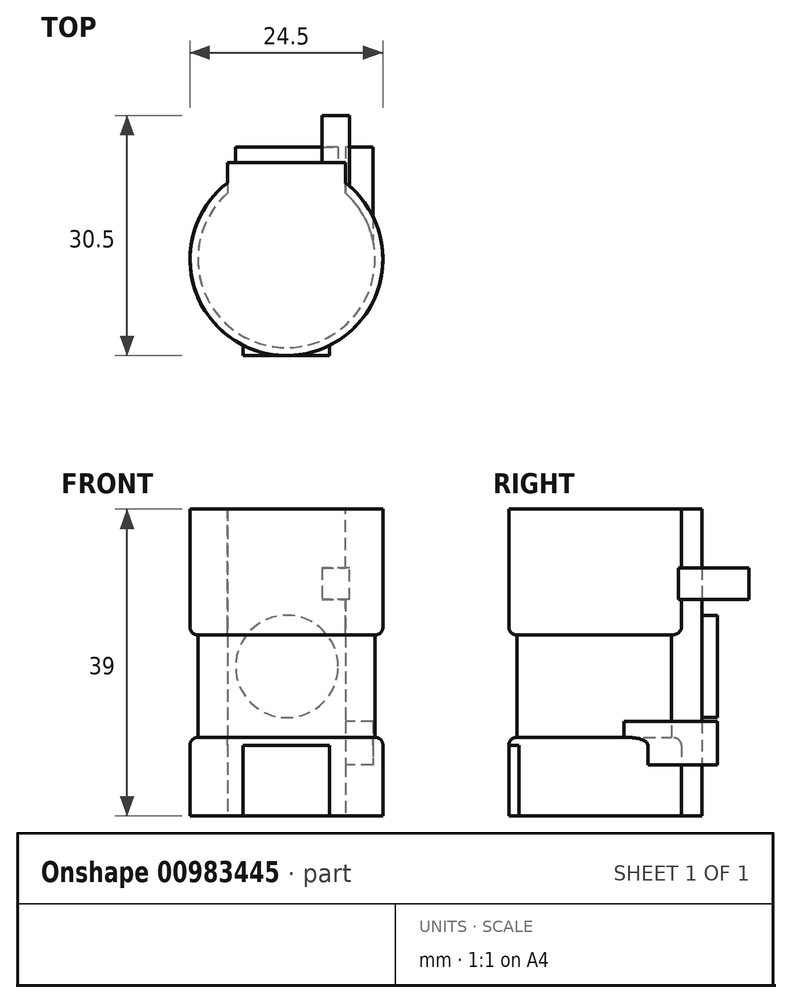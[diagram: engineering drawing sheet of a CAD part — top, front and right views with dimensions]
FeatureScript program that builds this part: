
annotation { "Feature Type Name" : "Feature", "Feature Type Description" : "" }
export const myFeature = defineFeature(function(context is Context, id is Id, definition is map)
    precondition{}
    {
        {
            var Q0;
            Q0=qCreatedBy(makeId("Top.planeOp"),FACE);
            var sketch = newSketch(context, id + "F0", { "sketchPlane" : qUnion([Q0])});
            skCircle(sketch, "E0", {"center": v(0, 0) * mm, "radius": 11.25 * mm});
            skSolve(sketch);
        }
        {
            var Q0;
            Q0 = qSketchRegion(id + "F0", true);
            extrude(context, id + "F1", {"entities" : qUnion([Q0]), "depth" : 39 * mm, "offsetDistance" : 25 * mm});
        }
        {
            var Q0;
            Q0=makeQuery(id+"F1.opExtrude","CAP_FACE",FACE,{"disambiguationData":[OSD([sQuery(id+"F0.wireOp",EDGE,"E0")])],"isStart":false});
            var sketch = newSketch(context, id + "F2", { "sketchPlane" : qUnion([Q0])});
            skCircle(sketch, "E1", {"center": v(0, 0) * mm, "radius": 12.25 * mm});
            skSolve(sketch);
        }
        {
            var Q0;
            Q0=makeQuery(id+"F2.imprint","IMPRINT",FACE,{"disambiguationData":[TD([[makeQuery(id+"F2.imprint","IMPRINT",EDGE,{"derivedFrom":sQuery(id+"F2.wireOp",EDGE,"E1")}),1.0]])]});
            extrude(context, id + "F3", {"entities" : qUnion([Q0]), "operationType" : NewBodyOperationType.ADD, "oppositeDirection" : true, "depth" : 16 * mm, "offsetDistance" : 25 * mm});
        }
        {
            var Q0;
            Q0=makeQuery(id+"F1.opExtrude","CAP_FACE",FACE,{"disambiguationData":[OSD([sQuery(id+"F0.wireOp",EDGE,"E0")])],"isStart":true});
            var sketch = newSketch(context, id + "F4", { "sketchPlane" : qUnion([Q0])});
            skCircle(sketch, "E2", {"center": v(0, 0) * mm, "radius": 12.25 * mm});
            skSolve(sketch);
        }
        {
            var Q0;
            Q0=makeQuery(id+"F3.opExtrude","CAP_EDGE",EDGE,{"disambiguationData":[OSD([sQuery(id+"F2.wireOp",EDGE,"E1")])],"isStart":false});
            fillet(context, id + "F5", {"entities" : qUnion([Q0]), "radius" : 1 * mm, "tangentPropagation" : true, "allowEdgeOverflow" : false});
        }
        {
            var Q0;
            Q0=makeQuery(id+"F4.imprint","IMPRINT",FACE,{"disambiguationData":[TD([[makeQuery(id+"F4.imprint","IMPRINT",EDGE,{"derivedFrom":sQuery(id+"F4.wireOp",EDGE,"E2")}),1.0]])]});
            extrude(context, id + "F6", {"entities" : qUnion([Q0]), "operationType" : NewBodyOperationType.ADD, "oppositeDirection" : true, "depth" : 10 * mm, "offsetDistance" : 25 * mm});
        }
        {
            var Q0;
            Q0=makeQuery(id+"F6.opExtrude","CAP_EDGE",EDGE,{"disambiguationData":[OSD([sQuery(id+"F4.wireOp",EDGE,"E2")])],"isStart":false});
            fillet(context, id + "F7", {"entities" : qUnion([Q0]), "radius" : 1 * mm, "tangentPropagation" : true, "allowEdgeOverflow" : false});
        }
        {
            var Q0;
            {var subQ0=sQuery(id+"F0.wireOp",EDGE,"E0");Q0=makeQuery(id+"F6.boolean.opBoolean","MERGE",FACE,{"derivedFrom":[makeQuery(id+"F1.opExtrude","CAP_FACE",FACE,{"disambiguationData":[OSD([subQ0])],"isStart":true}),makeQuery(id+"F6.opExtrude","CAP_FACE",FACE,{"disambiguationData":[OSD([subQ0,sQuery(id+"F4.wireOp",EDGE,"E2")])],"isStart":true})]});}
            var sketch = newSketch(context, id + "F8", { "sketchPlane" : qUnion([Q0])});
            skLineSegment(sketch, "E3.bottom", {"start": v(-5.5, 12.25) * mm, "end": v(5.5, 12.25) * mm});
            skLineSegment(sketch, "E3.top", {"start": v(-5.5, 10.25) * mm, "end": v(5.5, 10.25) * mm});
            skLineSegment(sketch, "E3.left", {"start": v(-5.5, 12.25) * mm, "end": v(-5.5, 10.25) * mm});
            skLineSegment(sketch, "E3.right", {"start": v(5.5, 12.25) * mm, "end": v(5.5, 10.25) * mm});
            skPoint(sketch, "E3.middle", {"position": v(0, 11.25) * mm});
            skSolve(sketch);
        }
        {
            var Q0;
            {var subQ0=sQuery(id+"F8.wireOp",EDGE,"E3.left");var subQ1=sQuery(id+"F8.wireOp",EDGE,"E3.bottom");var subQ2=makeQuery(id+"F8.imprint","INTERSECT",VERTEX,{"derivedFrom":[subQ1,subQ0]});Q0=makeQuery(id+"F8.imprint","IMPRINT",FACE,{"disambiguationData":[TD([[makeQuery(id+"F8.imprint","IMPRINT",EDGE,{"disambiguationData":[TD([[subQ2,-1.0]])],"derivedFrom":subQ1}),-1.0]])]});}
            var Q1;
            {var subQ0=sQuery(id+"F8.wireOp",EDGE,"E3.right");var subQ1=sQuery(id+"F8.wireOp",EDGE,"E3.bottom");var subQ2=makeQuery(id+"F8.imprint","INTERSECT",VERTEX,{"derivedFrom":[subQ1,subQ0]});Q1=makeQuery(id+"F8.imprint","IMPRINT",FACE,{"disambiguationData":[TD([[makeQuery(id+"F8.imprint","IMPRINT",EDGE,{"disambiguationData":[TD([[subQ2,1.0]])],"derivedFrom":subQ1}),-1.0]])]});}
            extrude(context, id + "F9", {"entities" : qUnion([Q0, Q1]), "operationType" : NewBodyOperationType.ADD, "oppositeDirection" : true, "depth" : 9 * mm, "offsetDistance" : 25 * mm});
        }
        {
            var Q0;
            {var subQ0=sQuery(id+"F8.wireOp",EDGE,"E3.bottom");var subQ1=sQuery(id+"F4.wireOp",EDGE,"E2");var subQ2=sQuery(id+"F0.wireOp",EDGE,"E0");Q0=makeQuery(id+"F9.boolean.opBoolean","MERGE",FACE,{"derivedFrom":[makeQuery(id+"F6.boolean.opBoolean","MERGE",FACE,{"derivedFrom":[makeQuery(id+"F1.opExtrude","CAP_FACE",FACE,{"disambiguationData":[OSD([subQ2])],"isStart":true}),makeQuery(id+"F6.opExtrude","CAP_FACE",FACE,{"disambiguationData":[OSD([subQ2,subQ1])],"isStart":true})]}),makeQuery(id+"F9.opExtrude","CAP_FACE",FACE,{"disambiguationData":[OSD([subQ1,subQ0,sQuery(id+"F8.wireOp",EDGE,"E3.left")])],"isStart":true}),makeQuery(id+"F9.opExtrude","CAP_FACE",FACE,{"disambiguationData":[OSD([subQ1,subQ0,sQuery(id+"F8.wireOp",EDGE,"E3.right")])],"isStart":true})]});}
            var sketch = newSketch(context, id + "F10", { "sketchPlane" : qUnion([Q0])});
            skLineSegment(sketch, "E4.bottom", {"start": v(-7.5, -8.25) * mm, "end": v(7.5, -8.25) * mm});
            skLineSegment(sketch, "E4.top", {"start": v(-7.5, -12.25) * mm, "end": v(7.5, -12.25) * mm});
            skLineSegment(sketch, "E4.left", {"start": v(-7.5, -8.25) * mm, "end": v(-7.5, -12.25) * mm});
            skLineSegment(sketch, "E4.right", {"start": v(7.5, -8.25) * mm, "end": v(7.5, -12.25) * mm});
            skPoint(sketch, "E4.middle", {"position": v(0, -10.25) * mm});
            skSolve(sketch);
        }
        {
            var Q0;
            {var subQ0=sQuery(id+"F10.wireOp",EDGE,"E4.right");var subQ1=sQuery(id+"F10.wireOp",EDGE,"E4.top");var subQ2=makeQuery(id+"F10.imprint","INTERSECT",VERTEX,{"derivedFrom":[subQ1,subQ0]});Q0=makeQuery(id+"F10.imprint","IMPRINT",FACE,{"disambiguationData":[TD([[makeQuery(id+"F10.imprint","IMPRINT",EDGE,{"disambiguationData":[TD([[subQ2,1.0]])],"derivedFrom":subQ1}),1.0]])]});}
            var Q1;
            {var subQ0=sQuery(id+"F10.wireOp",EDGE,"E4.left");var subQ1=sQuery(id+"F10.wireOp",EDGE,"E4.top");var subQ2=makeQuery(id+"F10.imprint","INTERSECT",VERTEX,{"derivedFrom":[subQ1,subQ0]});Q1=makeQuery(id+"F10.imprint","IMPRINT",FACE,{"disambiguationData":[TD([[makeQuery(id+"F10.imprint","IMPRINT",EDGE,{"disambiguationData":[TD([[subQ2,-1.0]])],"derivedFrom":subQ1}),1.0]])]});}
            var Q2;
            {var subQ4=sQuery(id+"F10.wireOp",EDGE,"E4.bottom");Q2=makeQuery(id+"F10.imprint","IMPRINT",FACE,{"disambiguationData":[TD([[makeQuery(id+"F10.imprint","IMPRINT",EDGE,{"derivedFrom":subQ4}),-1.0]])]});}
            extrude(context, id + "F11", {"entities" : qUnion([Q0, Q1, Q2]), "operationType" : NewBodyOperationType.ADD, "oppositeDirection" : true, "depth" : 39 * mm, "offsetDistance" : 25 * mm});
        }
        {
            var Q0;
            Q0=makeQuery(id+"F11.opExtrude","SWEPT_FACE",FACE,{"disambiguationData":[OSD([sQuery(id+"F10.wireOp",EDGE,"E4.top")])]});
            var sketch = newSketch(context, id + "F12", { "sketchPlane" : qUnion([Q0])});
            skLineSegment(sketch, "E5.bottom", {"start": v(-11, 12) * mm, "end": v(-7.5, 12) * mm});
            skLineSegment(sketch, "E5.top", {"start": v(-11, 6.5) * mm, "end": v(-7.5, 6.5) * mm});
            skLineSegment(sketch, "E5.left", {"start": v(-11, 12) * mm, "end": v(-11, 6.5) * mm});
            skLineSegment(sketch, "E5.right", {"start": v(-7.5, 12) * mm, "end": v(-7.5, 6.5) * mm});
            skSolve(sketch);
        }
        {
            var Q0;
            Q0=makeQuery(id+"F12.imprint","IMPRINT",FACE,{"disambiguationData":[TD([[makeQuery(id+"F12.imprint","IMPRINT",EDGE,{"derivedFrom":sQuery(id+"F12.wireOp",EDGE,"E5.bottom")}),-1.0]])]});
            extrude(context, id + "F13", {"entities" : qUnion([Q0]), "operationType" : NewBodyOperationType.ADD, "depth" : 2 * mm, "offsetDistance" : 25 * mm, "hasSecondDirection" : true, "secondDirectionOppositeDirection" : true, "secondDirectionDepth" : 12 * mm});
        }
        {
            var Q0;
            Q0=makeQuery(id+"F11.opExtrude","SWEPT_FACE",FACE,{"disambiguationData":[OSD([sQuery(id+"F10.wireOp",EDGE,"E4.top")])]});
            var sketch = newSketch(context, id + "F14", { "sketchPlane" : qUnion([Q0])});
            skCircle(sketch, "E6", {"center": v(-0.06, 19) * mm, "radius": 6.5 * mm});
            skSolve(sketch);
        }
        {
            var Q0;
            Q0=makeQuery(id+"F14.imprint","IMPRINT",FACE,{"disambiguationData":[TD([[makeQuery(id+"F14.imprint","IMPRINT",EDGE,{"derivedFrom":sQuery(id+"F14.wireOp",EDGE,"E6")}),1.0]])]});
            extrude(context, id + "F15", {"entities" : qUnion([Q0]), "operationType" : NewBodyOperationType.ADD, "depth" : 2 * mm, "offsetDistance" : 25 * mm});
        }
        {
            var Q0;
            Q0=makeQuery(id+"F11.opExtrude","SWEPT_FACE",FACE,{"disambiguationData":[OSD([sQuery(id+"F10.wireOp",EDGE,"E4.top")])]});
            var sketch = newSketch(context, id + "F16", { "sketchPlane" : qUnion([Q0])});
            skLineSegment(sketch, "E7.bottom", {"start": v(-8, 27.5) * mm, "end": v(-4.5, 27.5) * mm});
            skLineSegment(sketch, "E7.top", {"start": v(-8, 31.5) * mm, "end": v(-4.5, 31.5) * mm});
            skLineSegment(sketch, "E7.left", {"start": v(-8, 27.5) * mm, "end": v(-8, 31.5) * mm});
            skLineSegment(sketch, "E7.right", {"start": v(-4.5, 27.5) * mm, "end": v(-4.5, 31.5) * mm});
            skSolve(sketch);
        }
        {
            var Q0;
            Q0=makeQuery(id+"F16.imprint","IMPRINT",FACE,{"disambiguationData":[TD([[makeQuery(id+"F16.imprint","IMPRINT",EDGE,{"derivedFrom":sQuery(id+"F16.wireOp",EDGE,"E7.bottom")}),1.0]])]});
            var Q1;
            {var subQ2=sQuery(id+"F16.wireOp",EDGE,"E7.right");Q1=makeQuery(id+"F16.imprint","IMPRINT",FACE,{"disambiguationData":[TD([[makeQuery(id+"F16.imprint","IMPRINT",EDGE,{"derivedFrom":subQ2}),1.0]])]});}
            extrude(context, id + "F17", {"entities" : qUnion([Q0, Q1]), "operationType" : NewBodyOperationType.ADD, "depth" : 6 * mm, "offsetDistance" : 25 * mm, "hasSecondDirection" : true, "secondDirectionOppositeDirection" : true, "secondDirectionDepth" : 16.7 * mm});
        }
    });
